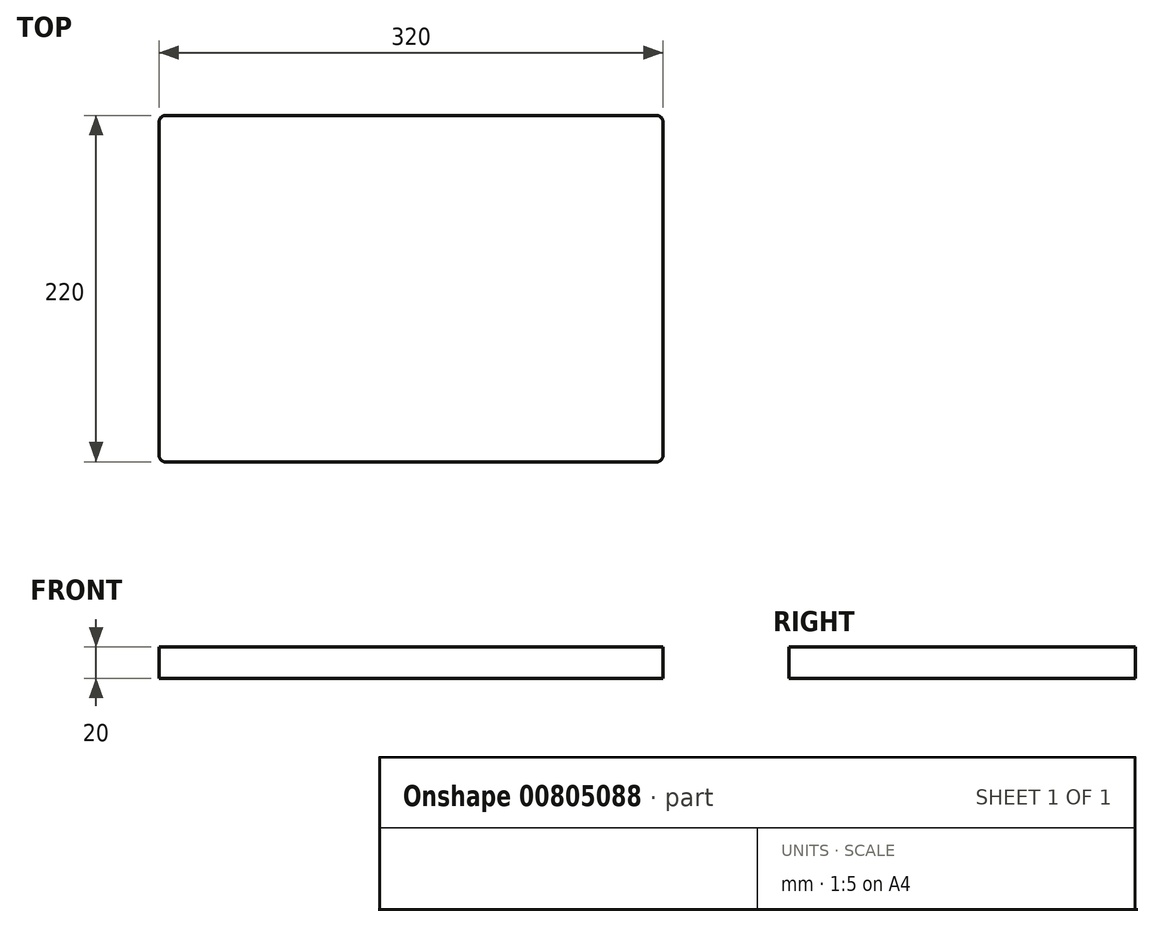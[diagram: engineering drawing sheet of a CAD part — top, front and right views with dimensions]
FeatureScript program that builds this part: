
annotation { "Feature Type Name" : "Feature", "Feature Type Description" : "" }
export const myFeature = defineFeature(function(context is Context, id is Id, definition is map)
    precondition{}
    {
        {
            var Q0;
            Q0=qCreatedBy(makeId("Top.planeOp"),FACE);
            var sketch = newSketch(context, id + "F0", { "sketchPlane" : qUnion([Q0])});
            skLineSegment(sketch, "E0.bottom", {"start": v(156, 110) * mm, "end": v(-156, 110) * mm});
            skLineSegment(sketch, "E0.top", {"start": v(156, -110) * mm, "end": v(-156, -110) * mm});
            skLineSegment(sketch, "E0.left", {"start": v(160, 106) * mm, "end": v(160, -106) * mm});
            skLineSegment(sketch, "E0.right", {"start": v(-160, 106) * mm, "end": v(-160, -106) * mm});
            skPoint(sketch, "E0.middle", {"position": v(0, 0) * mm});
            skPoint(sketch, "E1.visualSharp", {"position": v(-160, 110) * mm});
            skArc(sketch, "E1.filletArc", {"start": v(-156, 110) * mm, "mid": v(-158.83, 108.83) * mm, "end": v(-160, 106) * mm});
            skPoint(sketch, "E2.visualSharp", {"position": v(160, 110) * mm});
            skArc(sketch, "E2.filletArc", {"start": v(160, 106) * mm, "mid": v(158.83, 108.83) * mm, "end": v(156, 110) * mm});
            skPoint(sketch, "E3.visualSharp", {"position": v(160, -110) * mm});
            skArc(sketch, "E3.filletArc", {"start": v(156, -110) * mm, "mid": v(158.83, -108.83) * mm, "end": v(160, -106) * mm});
            skPoint(sketch, "E4.visualSharp", {"position": v(-160, -110) * mm});
            skArc(sketch, "E4.filletArc", {"start": v(-160, -106) * mm, "mid": v(-158.83, -108.83) * mm, "end": v(-156, -110) * mm});
            skSolve(sketch);
        }
        {
            var Q0;
            Q0 = qSketchRegion(id + "F0", true);
            extrude(context, id + "F1", {"entities" : qUnion([Q0]), "endBound" : BoundingType.SYMMETRIC, "depth" : 20 * mm, "offsetDistance" : 25 * mm});
        }
    });
